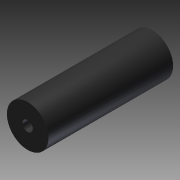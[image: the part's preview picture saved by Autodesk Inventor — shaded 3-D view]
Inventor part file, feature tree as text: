
AUTODESK INVENTOR PART (.ipt)
format: ipt  version: 2012 (Build 160160000, 160)  size: 74,240 bytes
history: native  units: in
note: dims shown in document units (in); Inventor stores cm internally (conversion verified against a paired STEP export)
features: extrude x1, sketch x1
ambient origin geometry x8: Origin, YZ Plane, XZ Plane, XY Plane, X Axis, Y Axis, Z Axis, Center Point
bodies: Solid1 (feature_tree)
feature tree (2):
  extrude  "Extrusion1"  Depth=2.0in
  sketch  "Sketch1"  dims[d0=0.5in d1=2.0in d2=6.0in d3=0.0in]
